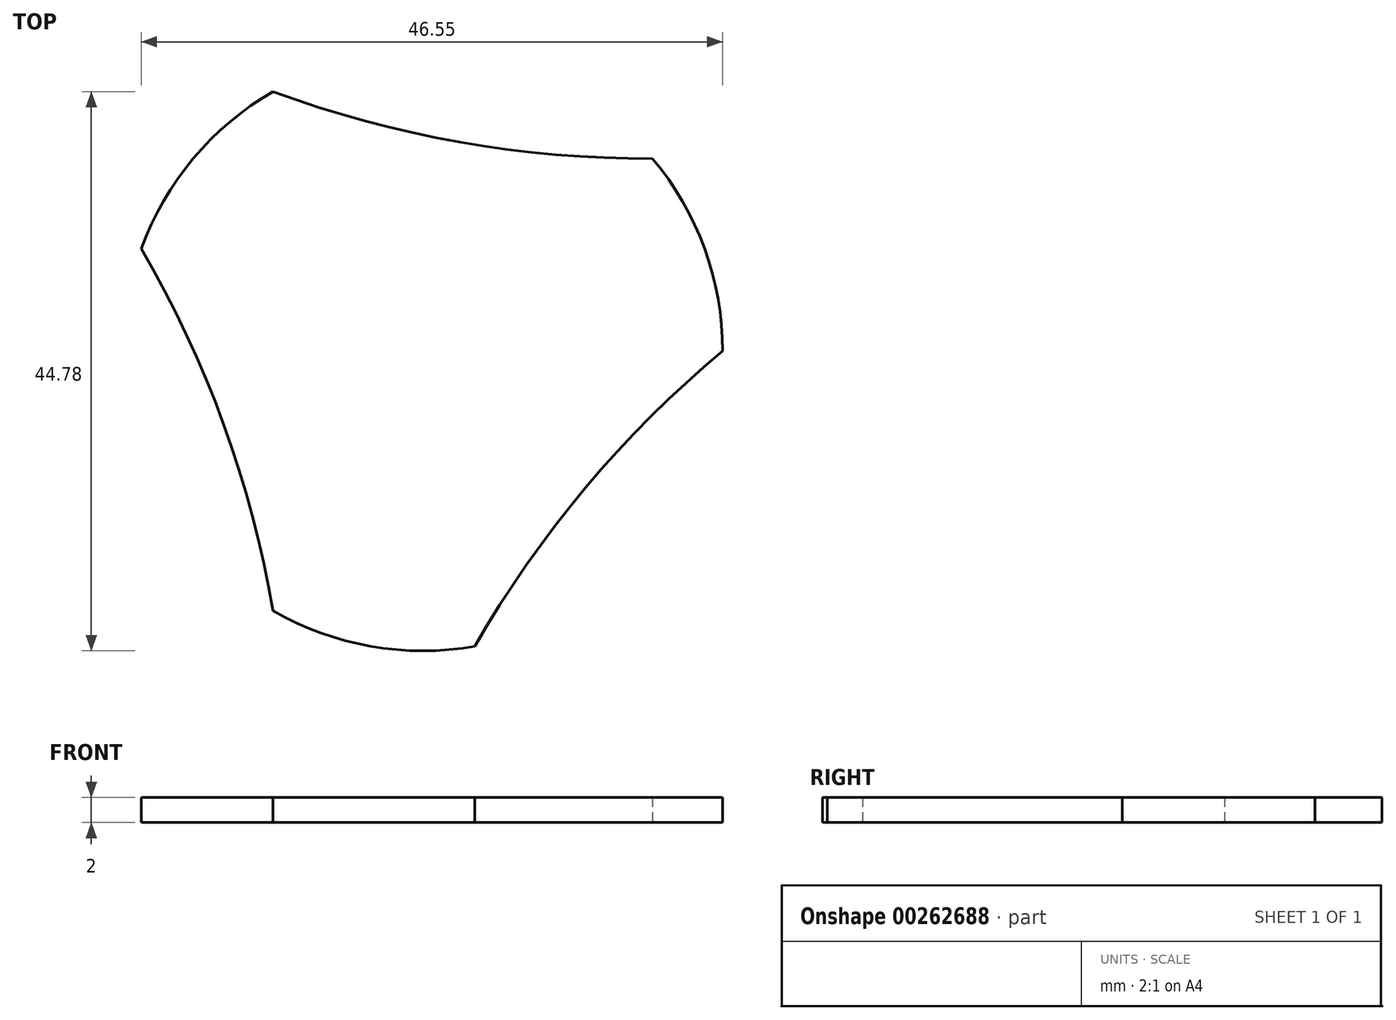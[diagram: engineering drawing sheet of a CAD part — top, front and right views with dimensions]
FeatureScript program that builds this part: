
annotation { "Feature Type Name" : "Feature", "Feature Type Description" : "" }
export const myFeature = defineFeature(function(context is Context, id is Id, definition is map)
    precondition{}
    {
        {
            var Q0;
            Q0=qCreatedBy(makeId("Top.planeOp"),FACE);
            var sketch = newSketch(context, id + "F0", { "sketchPlane" : qUnion([Q0])});
            skCircle(sketch, "E0", {"center": v(0, 0) * mm, "radius": 24 * mm, "construction": true});
            skArc(sketch, "E1", {"start": v(4.17, 23.64) * mm, "mid": v(12, 20.78) * mm, "end": v(18.39, 15.43) * mm, "construction": true});
            skLineSegment(sketch, "E2", {"start": v(0, 0) * mm, "end": v(4.17, 23.64) * mm, "construction": true});
            skLineSegment(sketch, "E3", {"start": v(0, 0) * mm, "end": v(18.39, 15.43) * mm, "construction": true});
            skLineSegment(sketch, "E4", {"start": v(0, 0) * mm, "end": v(24, 0) * mm, "construction": true});
            skLineSegment(sketch, "E5", {"start": v(0, 0) * mm, "end": v(18.39, -15.43) * mm, "construction": true});
            skLineSegment(sketch, "E6", {"start": v(0, 0) * mm, "end": v(4.17, -23.64) * mm, "construction": true});
            skLineSegment(sketch, "E7", {"start": v(0, 0) * mm, "end": v(-12, -20.78) * mm, "construction": true});
            skLineSegment(sketch, "E8", {"start": v(0, 0) * mm, "end": v(-22.55, -8.2) * mm, "construction": true});
            skLineSegment(sketch, "E9", {"start": v(0, 0) * mm, "end": v(-22.55, 8.2) * mm, "construction": true});
            skLineSegment(sketch, "E10", {"start": v(0, 0) * mm, "end": v(-12, 20.78) * mm, "construction": true});
            skArc(sketch, "E11", {"start": v(-12, 20.78) * mm, "mid": v(-18.39, 15.43) * mm, "end": v(-22.55, 8.2) * mm});
            skArc(sketch, "E12", {"start": v(-12, 20.78) * mm, "mid": v(2.95, 16.74) * mm, "end": v(18.39, 15.43) * mm});
            skArc(sketch, "E13", {"start": v(24, 0) * mm, "mid": v(22.55, 8.2) * mm, "end": v(18.39, 15.43) * mm});
            skArc(sketch, "E14", {"start": v(24, 0) * mm, "mid": v(13.02, -10.93) * mm, "end": v(4.17, -23.64) * mm});
            skArc(sketch, "E15", {"start": v(-12, -20.78) * mm, "mid": v(-4.17, -23.64) * mm, "end": v(4.17, -23.64) * mm});
            skArc(sketch, "E16", {"start": v(-12, -20.78) * mm, "mid": v(-15.97, -5.81) * mm, "end": v(-22.55, 8.2) * mm});
            skSolve(sketch);
        }
        {
            var Q0;
            Q0 = qSketchRegion(id + "F0", true);
            extrude(context, id + "F1", {"entities" : qUnion([Q0]), "depth" : 2 * mm});
        }
    });
